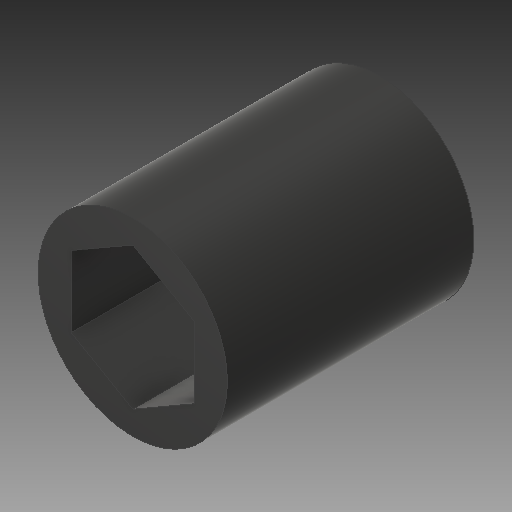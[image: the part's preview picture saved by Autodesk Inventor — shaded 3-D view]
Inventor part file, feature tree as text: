
AUTODESK INVENTOR PART (.ipt)
format: ipt  version: 2017 (Build 210142000, 142)  size: 106,496 bytes
history: native  units: in
note: dims shown in document units (in); Inventor stores cm internally (conversion verified against a paired STEP export)
features: extrude x1, sketch x1
ambient origin geometry x8: Origin, YZ Plane, XZ Plane, XY Plane, X Axis, Y Axis, Z Axis, Center Point
bodies: Solid1 (feature_tree)
feature tree (2):
  extrude  "Extrusion1"  Depth=1.0in
  sketch  "Sketch1"  dims[d0=0.5in d1=0.768in d2=1.0in d3=0.0in]
